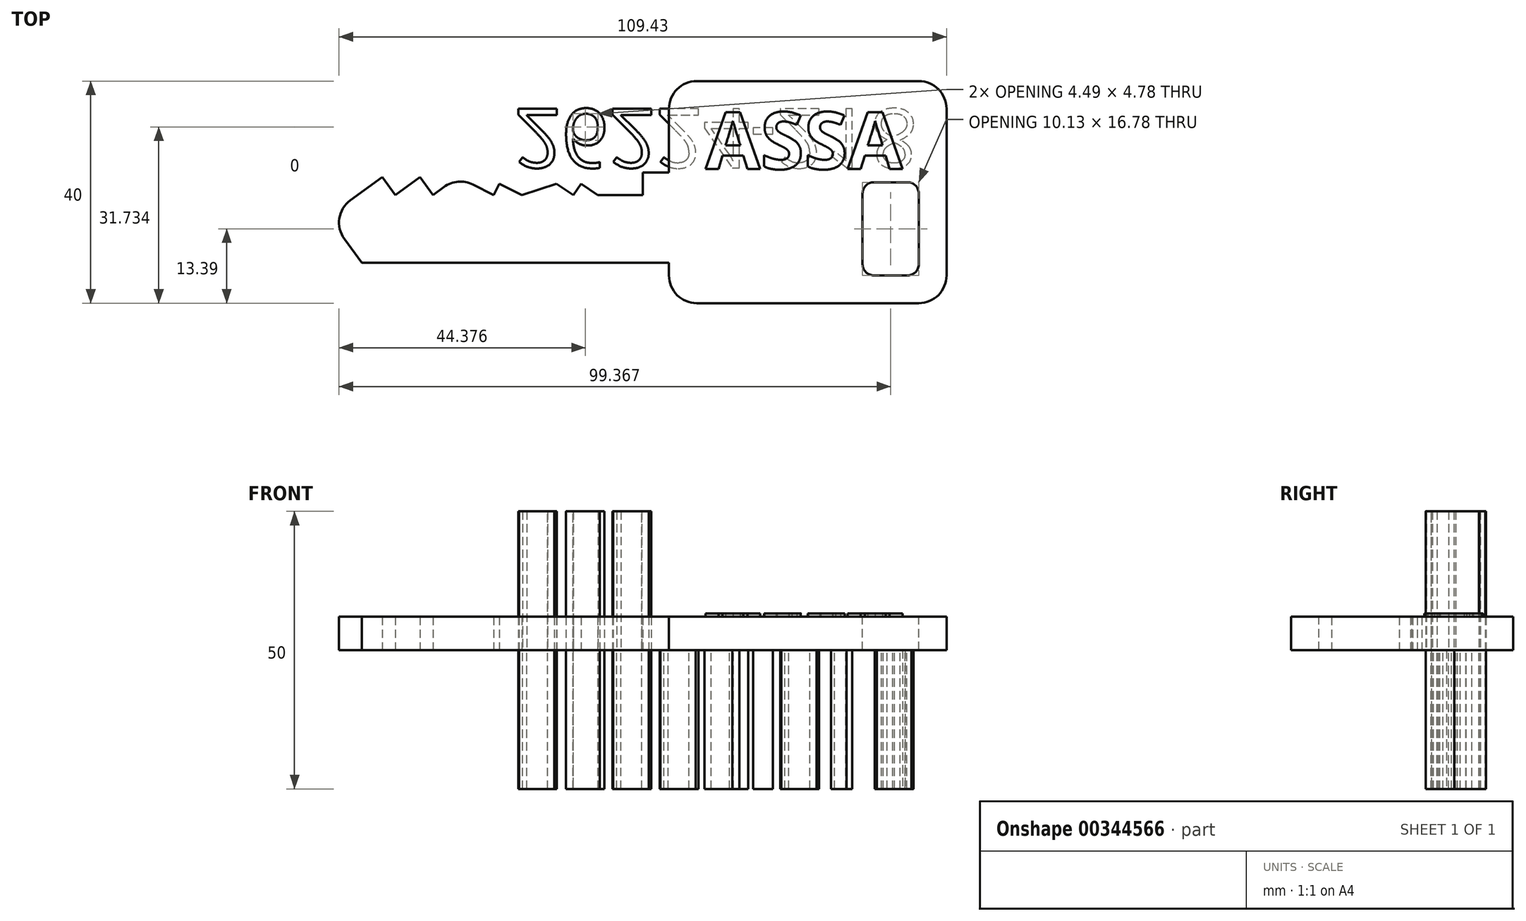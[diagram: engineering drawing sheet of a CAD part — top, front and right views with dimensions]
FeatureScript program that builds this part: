
annotation { "Feature Type Name" : "Feature", "Feature Type Description" : "" }
export const myFeature = defineFeature(function(context is Context, id is Id, definition is map)
    precondition{}
    {
        {
            var Q0;
            Q0=qCreatedBy(makeId("Top.planeOp"),FACE);
            var sketch = newSketch(context, id + "F0", { "sketchPlane" : qUnion([Q0])});
            skLineSegment(sketch, "E0", {"start": v(50, -21.47) * mm, "end": v(50, 8.53) * mm});
            skLineSegment(sketch, "E1", {"start": v(45, 13.53) * mm, "end": v(5, 13.53) * mm});
            skLineSegment(sketch, "E2", {"start": v(0, 8.53) * mm, "end": v(0, -2.92) * mm});
            skLineSegment(sketch, "E3", {"start": v(0, -2.92) * mm, "end": v(-4.7, -2.92) * mm});
            skLineSegment(sketch, "E4", {"start": v(-4.7, -2.92) * mm, "end": v(-4.7, -6.97) * mm});
            skLineSegment(sketch, "E5", {"start": v(-4.7, -6.97) * mm, "end": v(-12.8, -6.97) * mm});
            skLineSegment(sketch, "E6", {"start": v(-12.8, -6.97) * mm, "end": v(-15.85, -4.95) * mm});
            skLineSegment(sketch, "E7", {"start": v(-15.85, -4.95) * mm, "end": v(-17.2, -6.97) * mm});
            skLineSegment(sketch, "E8", {"start": v(-17.2, -6.97) * mm, "end": v(-20.25, -4.95) * mm});
            skLineSegment(sketch, "E9", {"start": v(-20.25, -4.95) * mm, "end": v(-26.5, -6.97) * mm});
            skLineSegment(sketch, "E10", {"start": v(-26.5, -6.97) * mm, "end": v(-30.56, -4.95) * mm});
            skLineSegment(sketch, "E11", {"start": v(-30.56, -4.95) * mm, "end": v(-31.58, -6.97) * mm});
            skLineSegment(sketch, "E12", {"start": v(-31.58, -6.97) * mm, "end": v(-35.33, -5.1) * mm});
            skLineSegment(sketch, "E13", {"start": v(-40.53, -5.54) * mm, "end": v(-42.48, -6.97) * mm});
            skLineSegment(sketch, "E14", {"start": v(-42.48, -6.97) * mm, "end": v(-44.87, -3.73) * mm});
            skLineSegment(sketch, "E15", {"start": v(-44.87, -3.73) * mm, "end": v(-49.28, -6.97) * mm});
            skLineSegment(sketch, "E16", {"start": v(-49.28, -6.97) * mm, "end": v(-51.67, -3.73) * mm});
            skLineSegment(sketch, "E17", {"start": v(-51.67, -3.73) * mm, "end": v(-57.39, -7.93) * mm});
            skLineSegment(sketch, "E18", {"start": v(-58.45, -14.92) * mm, "end": v(-55.31, -19.2) * mm});
            skLineSegment(sketch, "E19", {"start": v(-55.31, -19.2) * mm, "end": v(-4.7, -19.2) * mm});
            skLineSegment(sketch, "E20", {"start": v(-4.7, -19.2) * mm, "end": v(0, -19.2) * mm});
            skLineSegment(sketch, "E21", {"start": v(0, -19.2) * mm, "end": v(0, -21.47) * mm});
            skLineSegment(sketch, "E22", {"start": v(5, -26.47) * mm, "end": v(45, -26.47) * mm});
            skPoint(sketch, "E23.visualSharp", {"position": v(0, -26.47) * mm});
            skArc(sketch, "E23.filletArc", {"start": v(0, -21.47) * mm, "mid": v(1.46, -25) * mm, "end": v(5, -26.47) * mm});
            skPoint(sketch, "E24.visualSharp", {"position": v(50, -26.47) * mm});
            skArc(sketch, "E24.filletArc", {"start": v(45, -26.47) * mm, "mid": v(48.54, -25) * mm, "end": v(50, -21.47) * mm});
            skPoint(sketch, "E25.visualSharp", {"position": v(50, 13.53) * mm});
            skArc(sketch, "E25.filletArc", {"start": v(50, 8.53) * mm, "mid": v(48.54, 12.07) * mm, "end": v(45, 13.53) * mm});
            skPoint(sketch, "E26.visualSharp", {"position": v(0, 13.53) * mm});
            skArc(sketch, "E26.filletArc", {"start": v(5, 13.53) * mm, "mid": v(1.46, 12.07) * mm, "end": v(0, 8.53) * mm});
            skPoint(sketch, "E27.visualSharp", {"position": v(-61.42, -10.9) * mm});
            skArc(sketch, "E27.filletArc", {"start": v(-57.39, -7.93) * mm, "mid": v(-59.37, -11.2) * mm, "end": v(-58.45, -14.92) * mm});
            skPoint(sketch, "E28.visualSharp", {"position": v(-38.07, -3.73) * mm});
            skArc(sketch, "E28.filletArc", {"start": v(-35.33, -5.1) * mm, "mid": v(-38, -4.59) * mm, "end": v(-40.53, -5.54) * mm});
            skSolve(sketch);
        }
        {
            var Q0;
            Q0=makeQuery(id+"F0.imprint","IMPRINT",FACE,{"disambiguationData":[TD([[makeQuery(id+"F0.imprint","IMPRINT",EDGE,{"derivedFrom":sQuery(id+"F0.wireOp",EDGE,"E0")}),1.0]])]});
            extrude(context, id + "F1", {"entities" : qUnion([Q0]), "depth" : 6 * mm});
        }
        {
            var Q0;
            Q0=makeQuery(id+"F1.opExtrude","CAP_FACE",FACE,{"disambiguationData":[OSD([sQuery(id+"F0.wireOp",EDGE,"E0"),sQuery(id+"F0.wireOp",EDGE,"E1"),sQuery(id+"F0.wireOp",EDGE,"E2"),sQuery(id+"F0.wireOp",EDGE,"E3"),sQuery(id+"F0.wireOp",EDGE,"E4"),sQuery(id+"F0.wireOp",EDGE,"E5"),sQuery(id+"F0.wireOp",EDGE,"E6"),sQuery(id+"F0.wireOp",EDGE,"E7"),sQuery(id+"F0.wireOp",EDGE,"E8"),sQuery(id+"F0.wireOp",EDGE,"E9"),sQuery(id+"F0.wireOp",EDGE,"E10"),sQuery(id+"F0.wireOp",EDGE,"E11"),sQuery(id+"F0.wireOp",EDGE,"E12"),sQuery(id+"F0.wireOp",EDGE,"E13"),sQuery(id+"F0.wireOp",EDGE,"E14"),sQuery(id+"F0.wireOp",EDGE,"E15"),sQuery(id+"F0.wireOp",EDGE,"E16"),sQuery(id+"F0.wireOp",EDGE,"E17"),sQuery(id+"F0.wireOp",EDGE,"E18"),sQuery(id+"F0.wireOp",EDGE,"E19"),sQuery(id+"F0.wireOp",EDGE,"E20"),sQuery(id+"F0.wireOp",EDGE,"E21"),sQuery(id+"F0.wireOp",EDGE,"E22"),sQuery(id+"F0.wireOp",EDGE,"E23.filletArc"),sQuery(id+"F0.wireOp",EDGE,"E24.filletArc"),sQuery(id+"F0.wireOp",EDGE,"E25.filletArc"),sQuery(id+"F0.wireOp",EDGE,"E26.filletArc"),sQuery(id+"F0.wireOp",EDGE,"E27.filletArc"),sQuery(id+"F0.wireOp",EDGE,"E28.filletArc")])],"isStart":false});
            var sketch = newSketch(context, id + "F2", { "sketchPlane" : qUnion([Q0])});
            skLineSegment(sketch, "E29", {"start": v(45, -19.47) * mm, "end": v(45, -6.7) * mm});
            skLineSegment(sketch, "E30", {"start": v(43, -4.7) * mm, "end": v(36.87, -4.7) * mm});
            skLineSegment(sketch, "E31", {"start": v(34.87, -6.7) * mm, "end": v(34.87, -19.47) * mm});
            skLineSegment(sketch, "E32", {"start": v(36.87, -21.47) * mm, "end": v(43, -21.47) * mm});
            skPoint(sketch, "E33.visualSharp", {"position": v(34.87, -4.7) * mm});
            skArc(sketch, "E33.filletArc", {"start": v(36.87, -4.7) * mm, "mid": v(35.46, -5.28) * mm, "end": v(34.87, -6.7) * mm});
            skPoint(sketch, "E34.visualSharp", {"position": v(45, -4.7) * mm});
            skArc(sketch, "E34.filletArc", {"start": v(45, -6.7) * mm, "mid": v(44.41, -5.28) * mm, "end": v(43, -4.7) * mm});
            skPoint(sketch, "E35.visualSharp", {"position": v(45, -21.47) * mm});
            skArc(sketch, "E35.filletArc", {"start": v(43, -21.47) * mm, "mid": v(44.41, -20.88) * mm, "end": v(45, -19.47) * mm});
            skPoint(sketch, "E36.visualSharp", {"position": v(34.87, -21.47) * mm});
            skArc(sketch, "E36.filletArc", {"start": v(34.87, -19.47) * mm, "mid": v(35.46, -20.88) * mm, "end": v(36.87, -21.47) * mm});
            skSolve(sketch);
        }
        {
            var Q0;
            Q0=makeQuery(id+"F2.imprint","IMPRINT",FACE,{"disambiguationData":[TD([[makeQuery(id+"F2.imprint","IMPRINT",EDGE,{"derivedFrom":sQuery(id+"F2.wireOp",EDGE,"E29")}),1.0]])]});
            extrude(context, id + "F3", {"entities" : qUnion([Q0]), "operationType" : NewBodyOperationType.REMOVE, "oppositeDirection" : true, "depth" : 25 * mm});
        }
        {
            var Q0;
            Q0=makeQuery(id+"F1.opExtrude","CAP_FACE",FACE,{"disambiguationData":[OSD([sQuery(id+"F0.wireOp",EDGE,"E0"),sQuery(id+"F0.wireOp",EDGE,"E1"),sQuery(id+"F0.wireOp",EDGE,"E2"),sQuery(id+"F0.wireOp",EDGE,"E3"),sQuery(id+"F0.wireOp",EDGE,"E4"),sQuery(id+"F0.wireOp",EDGE,"E5"),sQuery(id+"F0.wireOp",EDGE,"E6"),sQuery(id+"F0.wireOp",EDGE,"E7"),sQuery(id+"F0.wireOp",EDGE,"E8"),sQuery(id+"F0.wireOp",EDGE,"E9"),sQuery(id+"F0.wireOp",EDGE,"E10"),sQuery(id+"F0.wireOp",EDGE,"E11"),sQuery(id+"F0.wireOp",EDGE,"E12"),sQuery(id+"F0.wireOp",EDGE,"E13"),sQuery(id+"F0.wireOp",EDGE,"E14"),sQuery(id+"F0.wireOp",EDGE,"E15"),sQuery(id+"F0.wireOp",EDGE,"E16"),sQuery(id+"F0.wireOp",EDGE,"E17"),sQuery(id+"F0.wireOp",EDGE,"E18"),sQuery(id+"F0.wireOp",EDGE,"E19"),sQuery(id+"F0.wireOp",EDGE,"E20"),sQuery(id+"F0.wireOp",EDGE,"E21"),sQuery(id+"F0.wireOp",EDGE,"E22"),sQuery(id+"F0.wireOp",EDGE,"E23.filletArc"),sQuery(id+"F0.wireOp",EDGE,"E24.filletArc"),sQuery(id+"F0.wireOp",EDGE,"E25.filletArc"),sQuery(id+"F0.wireOp",EDGE,"E26.filletArc"),sQuery(id+"F0.wireOp",EDGE,"E27.filletArc"),sQuery(id+"F0.wireOp",EDGE,"E28.filletArc")])],"isStart":false});
            var sketch = newSketch(context, id + "F4", { "sketchPlane" : qUnion([Q0])});
            skLineSegment(sketch, "E37", {"start": v(35.57, -2.92) * mm, "end": v(38.99, 6.59) * mm});
            skLineSegment(sketch, "E38", {"start": v(38.99, 6.59) * mm, "end": v(40.64, 6.59) * mm});
            skLineSegment(sketch, "E39", {"start": v(40.64, 6.59) * mm, "end": v(44.44, -2.92) * mm});
            skLineSegment(sketch, "E40", {"start": v(44.44, -2.92) * mm, "end": v(43.05, -2.92) * mm});
            skLineSegment(sketch, "E41", {"start": v(43.05, -2.92) * mm, "end": v(41.88, 0) * mm});
            skLineSegment(sketch, "E42", {"start": v(41.88, 0) * mm, "end": v(38.1, 0) * mm});
            skLineSegment(sketch, "E43", {"start": v(38.1, 0) * mm, "end": v(36.83, -2.92) * mm});
            skLineSegment(sketch, "E44", {"start": v(36.83, -2.92) * mm, "end": v(35.57, -2.92) * mm});
            skLineSegment(sketch, "E45", {"start": v(39.88, 4.56) * mm, "end": v(38.62, 1.84) * mm});
            skPoint(sketch, "E45.endSnap0", {"position": v(37.28, 1.84) * mm});
            skLineSegment(sketch, "E46", {"start": v(38.62, 1.84) * mm, "end": v(41.15, 1.84) * mm});
            skLineSegment(sketch, "E47", {"start": v(41.15, 1.84) * mm, "end": v(39.88, 4.56) * mm});
            skSolve(sketch);
        }
        {
            var Q0;
            Q0=makeQuery(id+"F4.imprint","IMPRINT",FACE,{"disambiguationData":[TD([[makeQuery(id+"F4.imprint","IMPRINT",EDGE,{"derivedFrom":sQuery(id+"F4.wireOp",EDGE,"E37")}),-1.0]])]});
            extrude(context, id + "F5", {"entities" : qUnion([Q0]), "operationType" : NewBodyOperationType.ADD, "oppositeDirection" : true, "depth" : 2 * mm});
        }
        {
            var Q0;
            Q0=makeQuery(id+"F1.opExtrude","CAP_FACE",FACE,{"disambiguationData":[OSD([sQuery(id+"F0.wireOp",EDGE,"E0"),sQuery(id+"F0.wireOp",EDGE,"E1"),sQuery(id+"F0.wireOp",EDGE,"E2"),sQuery(id+"F0.wireOp",EDGE,"E3"),sQuery(id+"F0.wireOp",EDGE,"E4"),sQuery(id+"F0.wireOp",EDGE,"E5"),sQuery(id+"F0.wireOp",EDGE,"E6"),sQuery(id+"F0.wireOp",EDGE,"E7"),sQuery(id+"F0.wireOp",EDGE,"E8"),sQuery(id+"F0.wireOp",EDGE,"E9"),sQuery(id+"F0.wireOp",EDGE,"E10"),sQuery(id+"F0.wireOp",EDGE,"E11"),sQuery(id+"F0.wireOp",EDGE,"E12"),sQuery(id+"F0.wireOp",EDGE,"E13"),sQuery(id+"F0.wireOp",EDGE,"E14"),sQuery(id+"F0.wireOp",EDGE,"E15"),sQuery(id+"F0.wireOp",EDGE,"E16"),sQuery(id+"F0.wireOp",EDGE,"E17"),sQuery(id+"F0.wireOp",EDGE,"E18"),sQuery(id+"F0.wireOp",EDGE,"E19"),sQuery(id+"F0.wireOp",EDGE,"E20"),sQuery(id+"F0.wireOp",EDGE,"E21"),sQuery(id+"F0.wireOp",EDGE,"E22"),sQuery(id+"F0.wireOp",EDGE,"E23.filletArc"),sQuery(id+"F0.wireOp",EDGE,"E24.filletArc"),sQuery(id+"F0.wireOp",EDGE,"E25.filletArc"),sQuery(id+"F0.wireOp",EDGE,"E26.filletArc"),sQuery(id+"F0.wireOp",EDGE,"E27.filletArc"),sQuery(id+"F0.wireOp",EDGE,"E28.filletArc")])],"isStart":false});
            var sketch = newSketch(context, id + "F6", { "sketchPlane" : qUnion([Q0])});
            skText(sketch, "E48", { "text": "ASSA\n", "fontName": "OpenSans-Bold.ttf"});
            const initialGuessF6  = {"E48": [0.00658, -0.0023, 1, 0, 0.0103]};
            skSetInitialGuess(sketch, initialGuessF6);
            skSolve(sketch);
        }
        {
            var Q0;
            Q0 = qSketchRegion(id + "F6", true);
            extrude(context, id + "F7", {"entities" : qUnion([Q0]), "operationType" : NewBodyOperationType.ADD, "depth" : 0.6 * mm});
        }
        {
            var Q0;
            Q0=makeQuery(id+"F1.opExtrude","CAP_FACE",FACE,{"disambiguationData":[OSD([sQuery(id+"F0.wireOp",EDGE,"E0"),sQuery(id+"F0.wireOp",EDGE,"E1"),sQuery(id+"F0.wireOp",EDGE,"E2"),sQuery(id+"F0.wireOp",EDGE,"E3"),sQuery(id+"F0.wireOp",EDGE,"E4"),sQuery(id+"F0.wireOp",EDGE,"E5"),sQuery(id+"F0.wireOp",EDGE,"E6"),sQuery(id+"F0.wireOp",EDGE,"E7"),sQuery(id+"F0.wireOp",EDGE,"E8"),sQuery(id+"F0.wireOp",EDGE,"E9"),sQuery(id+"F0.wireOp",EDGE,"E10"),sQuery(id+"F0.wireOp",EDGE,"E11"),sQuery(id+"F0.wireOp",EDGE,"E12"),sQuery(id+"F0.wireOp",EDGE,"E13"),sQuery(id+"F0.wireOp",EDGE,"E14"),sQuery(id+"F0.wireOp",EDGE,"E15"),sQuery(id+"F0.wireOp",EDGE,"E16"),sQuery(id+"F0.wireOp",EDGE,"E17"),sQuery(id+"F0.wireOp",EDGE,"E18"),sQuery(id+"F0.wireOp",EDGE,"E19"),sQuery(id+"F0.wireOp",EDGE,"E20"),sQuery(id+"F0.wireOp",EDGE,"E21"),sQuery(id+"F0.wireOp",EDGE,"E22"),sQuery(id+"F0.wireOp",EDGE,"E23.filletArc"),sQuery(id+"F0.wireOp",EDGE,"E24.filletArc"),sQuery(id+"F0.wireOp",EDGE,"E25.filletArc"),sQuery(id+"F0.wireOp",EDGE,"E26.filletArc"),sQuery(id+"F0.wireOp",EDGE,"E27.filletArc"),sQuery(id+"F0.wireOp",EDGE,"E28.filletArc")])],"isStart":true});
            var sketch = newSketch(context, id + "F8", { "sketchPlane" : qUnion([Q0])});
            skText(sketch, "E49", { "text": "26224-218", "fontName": "OpenSans-Regular.ttf"});
            const initialGuessF8  = {"E49": [-0.02787, -0.00853, 1, 0, 0.01069]};
            skSetInitialGuess(sketch, initialGuessF8);
            skSolve(sketch);
        }
        {
            var Q0;
            Q0 = qSketchRegion(id + "F8", true);
            extrude(context, id + "F9", {"entities" : qUnion([Q0]), "operationType" : NewBodyOperationType.ADD, "depth" : 25 * mm});
        }
        {
            var Q0;
            Q0=makeQuery(id+"F9.opExtrude","SWEPT_BODY",BODY,{"disambiguationData":[OSD([sQuery(id+"F8.wireOp",EDGE,"E49.sketch_text.stroke-0"),sQuery(id+"F8.wireOp",EDGE,"E49.sketch_text.stroke-1"),sQuery(id+"F8.wireOp",EDGE,"E49.sketch_text.stroke-2"),sQuery(id+"F8.wireOp",EDGE,"E49.sketch_text.stroke-3"),sQuery(id+"F8.wireOp",EDGE,"E49.sketch_text.stroke-4"),sQuery(id+"F8.wireOp",EDGE,"E49.sketch_text.stroke-5"),sQuery(id+"F8.wireOp",EDGE,"E49.sketch_text.stroke-6"),sQuery(id+"F8.wireOp",EDGE,"E49.sketch_text.stroke-7"),sQuery(id+"F8.wireOp",EDGE,"E49.sketch_text.stroke-8"),sQuery(id+"F8.wireOp",EDGE,"E49.sketch_text.stroke-9"),sQuery(id+"F8.wireOp",EDGE,"E49.sketch_text.stroke-10"),sQuery(id+"F8.wireOp",EDGE,"E49.sketch_text.stroke-11"),sQuery(id+"F8.wireOp",EDGE,"E49.sketch_text.stroke-12"),sQuery(id+"F8.wireOp",EDGE,"E49.sketch_text.stroke-13"),sQuery(id+"F8.wireOp",EDGE,"E49.sketch_text.stroke-14"),sQuery(id+"F8.wireOp",EDGE,"E49.sketch_text.stroke-15"),sQuery(id+"F8.wireOp",EDGE,"E49.sketch_text.stroke-16"),sQuery(id+"F8.wireOp",EDGE,"E49.sketch_text.stroke-17"),sQuery(id+"F8.wireOp",EDGE,"E49.sketch_text.stroke-18"),sQuery(id+"F8.wireOp",EDGE,"E49.sketch_text.stroke-19")])]});
            var Q1;
            Q1=makeQuery(id+"F9.opExtrude","SWEPT_BODY",BODY,{"disambiguationData":[OSD([sQuery(id+"F8.wireOp",EDGE,"E49.sketch_text.stroke-20"),sQuery(id+"F8.wireOp",EDGE,"E49.sketch_text.stroke-21"),sQuery(id+"F8.wireOp",EDGE,"E49.sketch_text.stroke-22"),sQuery(id+"F8.wireOp",EDGE,"E49.sketch_text.stroke-23"),sQuery(id+"F8.wireOp",EDGE,"E49.sketch_text.stroke-24"),sQuery(id+"F8.wireOp",EDGE,"E49.sketch_text.stroke-25"),sQuery(id+"F8.wireOp",EDGE,"E49.sketch_text.stroke-26"),sQuery(id+"F8.wireOp",EDGE,"E49.sketch_text.stroke-27"),sQuery(id+"F8.wireOp",EDGE,"E49.sketch_text.stroke-28"),sQuery(id+"F8.wireOp",EDGE,"E49.sketch_text.stroke-29"),sQuery(id+"F8.wireOp",EDGE,"E49.sketch_text.stroke-30"),sQuery(id+"F8.wireOp",EDGE,"E49.sketch_text.stroke-31"),sQuery(id+"F8.wireOp",EDGE,"E49.sketch_text.stroke-32"),sQuery(id+"F8.wireOp",EDGE,"E49.sketch_text.stroke-33"),sQuery(id+"F8.wireOp",EDGE,"E49.sketch_text.stroke-34"),sQuery(id+"F8.wireOp",EDGE,"E49.sketch_text.stroke-35"),sQuery(id+"F8.wireOp",EDGE,"E49.sketch_text.stroke-36"),sQuery(id+"F8.wireOp",EDGE,"E49.sketch_text.stroke-37"),sQuery(id+"F8.wireOp",EDGE,"E49.sketch_text.stroke-38"),sQuery(id+"F8.wireOp",EDGE,"E49.sketch_text.stroke-39"),sQuery(id+"F8.wireOp",EDGE,"E49.sketch_text.stroke-40"),sQuery(id+"F8.wireOp",EDGE,"E49.sketch_text.stroke-41"),sQuery(id+"F8.wireOp",EDGE,"E49.sketch_text.stroke-42"),sQuery(id+"F8.wireOp",EDGE,"E49.sketch_text.stroke-43"),sQuery(id+"F8.wireOp",EDGE,"E49.sketch_text.stroke-44")])]});
            var Q2;
            Q2=makeQuery(id+"F9.opExtrude","SWEPT_BODY",BODY,{"disambiguationData":[OSD([sQuery(id+"F8.wireOp",EDGE,"E49.sketch_text.stroke-45"),sQuery(id+"F8.wireOp",EDGE,"E49.sketch_text.stroke-46"),sQuery(id+"F8.wireOp",EDGE,"E49.sketch_text.stroke-47"),sQuery(id+"F8.wireOp",EDGE,"E49.sketch_text.stroke-48"),sQuery(id+"F8.wireOp",EDGE,"E49.sketch_text.stroke-49"),sQuery(id+"F8.wireOp",EDGE,"E49.sketch_text.stroke-50"),sQuery(id+"F8.wireOp",EDGE,"E49.sketch_text.stroke-51"),sQuery(id+"F8.wireOp",EDGE,"E49.sketch_text.stroke-52"),sQuery(id+"F8.wireOp",EDGE,"E49.sketch_text.stroke-53"),sQuery(id+"F8.wireOp",EDGE,"E49.sketch_text.stroke-54"),sQuery(id+"F8.wireOp",EDGE,"E49.sketch_text.stroke-55"),sQuery(id+"F8.wireOp",EDGE,"E49.sketch_text.stroke-56"),sQuery(id+"F8.wireOp",EDGE,"E49.sketch_text.stroke-57"),sQuery(id+"F8.wireOp",EDGE,"E49.sketch_text.stroke-58"),sQuery(id+"F8.wireOp",EDGE,"E49.sketch_text.stroke-59"),sQuery(id+"F8.wireOp",EDGE,"E49.sketch_text.stroke-60"),sQuery(id+"F8.wireOp",EDGE,"E49.sketch_text.stroke-61"),sQuery(id+"F8.wireOp",EDGE,"E49.sketch_text.stroke-62"),sQuery(id+"F8.wireOp",EDGE,"E49.sketch_text.stroke-63"),sQuery(id+"F8.wireOp",EDGE,"E49.sketch_text.stroke-64")])]});
            var Q3;
            Q3=qCreatedBy(makeId("Top.planeOp"),FACE);
            mirror(context, id + "F10", {"entities" : qUnion([Q0, Q1, Q2]), "mirrorPlane" : qUnion([Q3])});
        }
    });
